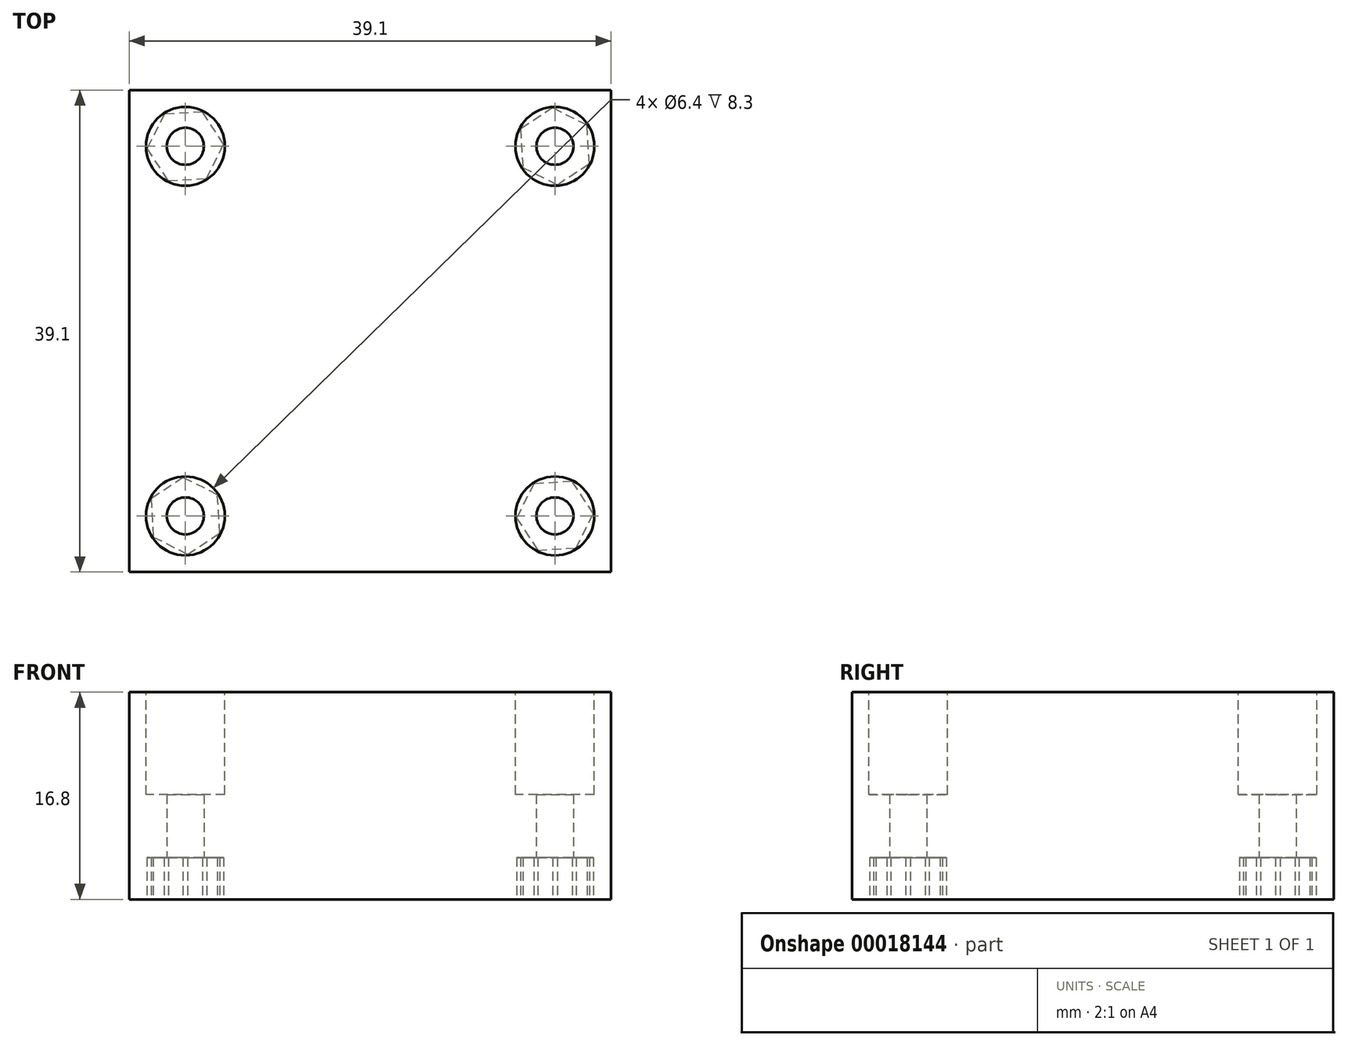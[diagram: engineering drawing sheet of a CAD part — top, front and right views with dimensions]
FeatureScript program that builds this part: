
annotation { "Feature Type Name" : "Feature", "Feature Type Description" : "" }
export const myFeature = defineFeature(function(context is Context, id is Id, definition is map)
    precondition{}
    {
        {
            var Q0;
            Q0=qCreatedBy(makeId("Top.planeOp"),FACE);
            var sketch = newSketch(context, id + "F0", { "sketchPlane" : qUnion([Q0])});
            skLineSegment(sketch, "E0.rect.bottom", {"start": v(-19.55, 19.55) * mm, "end": v(19.55, 19.55) * mm});
            skLineSegment(sketch, "E0.rect.top", {"start": v(-19.55, -19.55) * mm, "end": v(19.55, -19.55) * mm});
            skLineSegment(sketch, "E0.rect.left", {"start": v(-19.55, 19.55) * mm, "end": v(-19.55, -19.55) * mm});
            skLineSegment(sketch, "E0.rect.right", {"start": v(19.55, 19.55) * mm, "end": v(19.55, -19.55) * mm});
            skPoint(sketch, "E0.rect.middle", {"position": v(0, 0) * mm});
            skCircle(sketch, "E1", {"center": v(0, 0) * mm, "radius": 21.2 * mm, "construction": true});
            skLineSegment(sketch, "E2", {"start": v(19.55, 19.55) * mm, "end": v(-19.55, -19.55) * mm, "construction": true});
            skLineSegment(sketch, "E3", {"start": v(19.55, -19.55) * mm, "end": v(-19.55, 19.55) * mm, "construction": true});
            skCircle(sketch, "E4", {"center": v(-15, 15) * mm, "radius": 1.5 * mm});
            skLineSegment(sketch, "E5", {"start": v(0, 19.55) * mm, "end": v(0, -19.55) * mm, "construction": true});
            skLineSegment(sketch, "E6", {"start": v(-19.55, 0) * mm, "end": v(19.55, 0) * mm, "construction": true});
            skCircle(sketch, "E7.1.0", {"center": v(-15, -15) * mm, "radius": 1.5 * mm});
            skCircle(sketch, "E7.2.0", {"center": v(15, -15) * mm, "radius": 1.5 * mm});
            skCircle(sketch, "E7.3.0", {"center": v(15, 15) * mm, "radius": 1.5 * mm});
            skSolve(sketch);
        }
        {
            var Q0;
            Q0=makeQuery(id+"F0.imprint","IMPRINT",FACE,{"disambiguationData":[TD([[makeQuery(id+"F0.imprint","IMPRINT",EDGE,{"derivedFrom":sQuery(id+"F0.wireOp",EDGE,"E0.rect.bottom")}),-1.0]])]});
            extrude(context, id + "F1", {"entities" : qUnion([Q0]), "depth" : 16.8 * mm});
        }
        {
            var Q0;
            Q0=makeQuery(id+"F1.opExtrude","CAP_FACE",FACE,{"disambiguationData":[OSD([sQuery(id+"F0.wireOp",EDGE,"E0.rect.bottom"),sQuery(id+"F0.wireOp",EDGE,"E0.rect.top"),sQuery(id+"F0.wireOp",EDGE,"E0.rect.left"),sQuery(id+"F0.wireOp",EDGE,"E0.rect.right"),sQuery(id+"F0.wireOp",EDGE,"E4"),sQuery(id+"F0.wireOp",EDGE,"E7.1.0"),sQuery(id+"F0.wireOp",EDGE,"E7.2.0"),sQuery(id+"F0.wireOp",EDGE,"E7.3.0")])],"isStart":false});
            var sketch = newSketch(context, id + "F2", { "sketchPlane" : qUnion([Q0])});
            skCircle(sketch, "E8", {"center": v(-15, 15) * mm, "radius": 3.2 * mm});
            skCircle(sketch, "E9.1.0", {"center": v(-15, -15) * mm, "radius": 3.2 * mm});
            skCircle(sketch, "E9.2.0", {"center": v(15, -15) * mm, "radius": 3.2 * mm});
            skCircle(sketch, "E9.3.0", {"center": v(15, 15) * mm, "radius": 3.2 * mm});
            skPoint(sketch, "E9.center", {"position": v(0, 0) * mm});
            skSolve(sketch);
        }
        {
            var Q0;
            Q0 = qSketchRegion(id + "F2", true);
            extrude(context, id + "F3", {"entities" : qUnion([Q0]), "operationType" : NewBodyOperationType.REMOVE, "oppositeDirection" : true, "depth" : 8.3 * mm});
        }
        {
            var Q0;
            Q0=makeQuery(id+"F1.opExtrude","CAP_FACE",FACE,{"disambiguationData":[OSD([sQuery(id+"F0.wireOp",EDGE,"E0.rect.bottom"),sQuery(id+"F0.wireOp",EDGE,"E0.rect.top"),sQuery(id+"F0.wireOp",EDGE,"E0.rect.left"),sQuery(id+"F0.wireOp",EDGE,"E0.rect.right"),sQuery(id+"F0.wireOp",EDGE,"E4"),sQuery(id+"F0.wireOp",EDGE,"E7.1.0"),sQuery(id+"F0.wireOp",EDGE,"E7.2.0"),sQuery(id+"F0.wireOp",EDGE,"E7.3.0")])],"isStart":true});
            var sketch = newSketch(context, id + "F4", { "sketchPlane" : qUnion([Q0])});
            skCircle(sketch, "E10.cCircle", {"center": v(-15, -15) * mm, "radius": 2.7 * mm, "construction": true});
            skLineSegment(sketch, "E10.0", {"start": v(-13.27, -12.39) * mm, "end": v(-11.88, -15.18) * mm});
            skLineSegment(sketch, "E10.1", {"start": v(-11.88, -15.18) * mm, "end": v(-13.6, -17.78) * mm});
            skLineSegment(sketch, "E10.2", {"start": v(-13.6, -17.78) * mm, "end": v(-16.7, -17.6) * mm});
            skLineSegment(sketch, "E10.3", {"start": v(-16.7, -17.6) * mm, "end": v(-18.1, -14.8) * mm});
            skLineSegment(sketch, "E10.4", {"start": v(-18.1, -14.8) * mm, "end": v(-16.38, -12.2) * mm});
            skLineSegment(sketch, "E10.5", {"start": v(-16.38, -12.2) * mm, "end": v(-13.27, -12.39) * mm});
            skPoint(sketch, "E10.0.midPoint", {"position": v(-12.58, -13.78) * mm});
            skPoint(sketch, "E11.1.6", {"position": v(13.78, -12.58) * mm});
            skCircle(sketch, "E11.1.7", {"center": v(15, -15) * mm, "radius": 2.7 * mm, "construction": true});
            skLineSegment(sketch, "E11.1.8", {"start": v(12.39, -13.27) * mm, "end": v(15.18, -11.88) * mm});
            skLineSegment(sketch, "E11.1.10", {"start": v(15.18, -11.88) * mm, "end": v(17.78, -13.6) * mm});
            skLineSegment(sketch, "E11.1.12", {"start": v(17.78, -13.6) * mm, "end": v(17.6, -16.7) * mm});
            skLineSegment(sketch, "E11.1.14", {"start": v(17.6, -16.7) * mm, "end": v(14.8, -18.1) * mm});
            skLineSegment(sketch, "E11.1.16", {"start": v(14.8, -18.1) * mm, "end": v(12.2, -16.38) * mm});
            skLineSegment(sketch, "E11.1.18", {"start": v(12.2, -16.38) * mm, "end": v(12.39, -13.27) * mm});
            skPoint(sketch, "E11.2.6", {"position": v(12.58, 13.78) * mm});
            skCircle(sketch, "E11.2.7", {"center": v(15, 15) * mm, "radius": 2.7 * mm, "construction": true});
            skLineSegment(sketch, "E11.2.8", {"start": v(13.27, 12.39) * mm, "end": v(11.88, 15.18) * mm});
            skLineSegment(sketch, "E11.2.10", {"start": v(11.88, 15.18) * mm, "end": v(13.6, 17.78) * mm});
            skLineSegment(sketch, "E11.2.12", {"start": v(13.6, 17.78) * mm, "end": v(16.7, 17.6) * mm});
            skLineSegment(sketch, "E11.2.14", {"start": v(16.7, 17.6) * mm, "end": v(18.1, 14.8) * mm});
            skLineSegment(sketch, "E11.2.16", {"start": v(18.1, 14.8) * mm, "end": v(16.38, 12.2) * mm});
            skLineSegment(sketch, "E11.2.18", {"start": v(16.38, 12.2) * mm, "end": v(13.27, 12.39) * mm});
            skPoint(sketch, "E11.3.6", {"position": v(-13.78, 12.58) * mm});
            skCircle(sketch, "E11.3.7", {"center": v(-15, 15) * mm, "radius": 2.7 * mm, "construction": true});
            skLineSegment(sketch, "E11.3.8", {"start": v(-12.39, 13.27) * mm, "end": v(-15.18, 11.88) * mm});
            skLineSegment(sketch, "E11.3.10", {"start": v(-15.18, 11.88) * mm, "end": v(-17.78, 13.6) * mm});
            skLineSegment(sketch, "E11.3.12", {"start": v(-17.78, 13.6) * mm, "end": v(-17.6, 16.7) * mm});
            skLineSegment(sketch, "E11.3.14", {"start": v(-17.6, 16.7) * mm, "end": v(-14.8, 18.1) * mm});
            skLineSegment(sketch, "E11.3.16", {"start": v(-14.8, 18.1) * mm, "end": v(-12.2, 16.38) * mm});
            skLineSegment(sketch, "E11.3.18", {"start": v(-12.2, 16.38) * mm, "end": v(-12.39, 13.27) * mm});
            skPoint(sketch, "E11.center", {"position": v(0, 0) * mm});
            skSolve(sketch);
        }
        {
            var Q0;
            Q0 = qSketchRegion(id + "F4", true);
            extrude(context, id + "F5", {"entities" : qUnion([Q0]), "operationType" : NewBodyOperationType.REMOVE, "oppositeDirection" : true, "depth" : 3.4 * mm});
        }
    });
